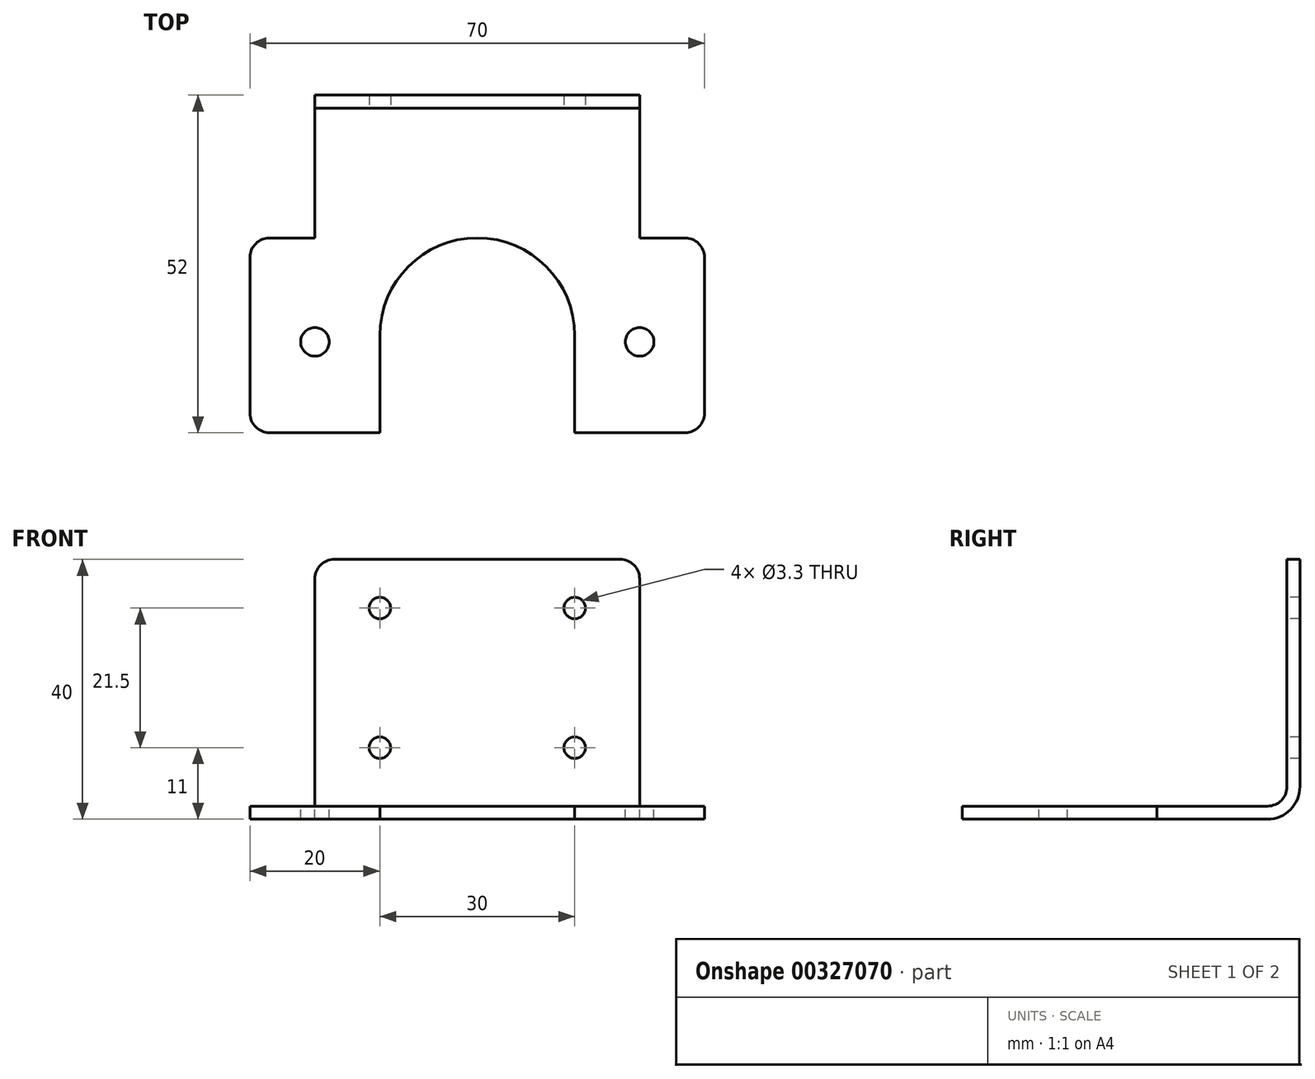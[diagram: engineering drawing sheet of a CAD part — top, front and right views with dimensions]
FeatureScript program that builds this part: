
annotation { "Feature Type Name" : "Feature", "Feature Type Description" : "" }
export const myFeature = defineFeature(function(context is Context, id is Id, definition is map)
    precondition{}
    {
        {
            var Q0;
            Q0=qCreatedBy(makeId("Right.planeOp"),FACE);
            var sketch = newSketch(context, id + "F0", { "sketchPlane" : qUnion([Q0])});
            skLineSegment(sketch, "E0", {"start": v(0, 5) * mm, "end": v(0, 40) * mm});
            skLineSegment(sketch, "E1", {"start": v(-5, 0) * mm, "end": v(-52, 0) * mm});
            skPoint(sketch, "E2.visualSharp", {"position": v(0, 0) * mm});
            skArc(sketch, "E2.filletArc", {"start": v(-5, 0) * mm, "mid": v(-1.46, 1.46) * mm, "end": v(0, 5) * mm});
            skLineSegment(sketch, "E3.0", {"start": v(-2, 5) * mm, "end": v(-2, 40) * mm});
            skArc(sketch, "E3.1", {"start": v(-5, 2) * mm, "mid": v(-2.88, 2.88) * mm, "end": v(-2, 5) * mm});
            skLineSegment(sketch, "E3.2", {"start": v(-5, 2) * mm, "end": v(-52, 2) * mm});
            skLineSegment(sketch, "E4", {"start": v(-52, 2) * mm, "end": v(-52, 0) * mm});
            skLineSegment(sketch, "E5", {"start": v(-2, 40) * mm, "end": v(0, 40) * mm});
            skSolve(sketch);
        }
        {
            var Q0;
            Q0=makeQuery(id+"F0.imprint","IMPRINT",FACE,{"disambiguationData":[TD([[makeQuery(id+"F0.imprint","IMPRINT",EDGE,{"derivedFrom":sQuery(id+"F0.wireOp",EDGE,"E0")}),1.0]])]});
            extrude(context, id + "F1", {"entities" : qUnion([Q0]), "depth" : 50 * mm, "symmetric" : true});
        }
        {
            var Q0;
            Q0=makeQuery(id+"F1.opExtrude","SWEPT_FACE",FACE,{"disambiguationData":[OSD([sQuery(id+"F0.wireOp",EDGE,"E3.0")])]});
            var sketch = newSketch(context, id + "F2", { "sketchPlane" : qUnion([Q0])});
            skLineSegment(sketch, "E6.bottom", {"start": v(15, 32.5) * mm, "end": v(-15, 32.5) * mm});
            skLineSegment(sketch, "E6.top", {"start": v(15, 11) * mm, "end": v(-15, 11) * mm});
            skLineSegment(sketch, "E6.left", {"start": v(15, 32.5) * mm, "end": v(15, 11) * mm});
            skLineSegment(sketch, "E6.right", {"start": v(-15, 32.5) * mm, "end": v(-15, 11) * mm});
            skPoint(sketch, "E6.middle", {"position": v(0, 21.75) * mm});
            skSolve(sketch);
        }
        {
            var Q0;
            Q0=sQuery(id+"F2.wireOp",VERTEX,"E6.right.start");
            var Q1;
            Q1=sQuery(id+"F2.wireOp",VERTEX,"E6.top.end");
            var Q2;
            Q2=sQuery(id+"F2.wireOp",VERTEX,"E6.left.end");
            var Q3;
            Q3=sQuery(id+"F2.wireOp",VERTEX,"E6.left.start");
            var Q4;
            Q4=makeQuery(id+"F1.opExtrude","SWEPT_BODY",BODY,{"disambiguationData":[OSD([sQuery(id+"F0.wireOp",EDGE,"E0"),sQuery(id+"F0.wireOp",EDGE,"E1"),sQuery(id+"F0.wireOp",EDGE,"E2.filletArc"),sQuery(id+"F0.wireOp",EDGE,"E3.0"),sQuery(id+"F0.wireOp",EDGE,"E3.1"),sQuery(id+"F0.wireOp",EDGE,"E3.2"),sQuery(id+"F0.wireOp",EDGE,"E4"),sQuery(id+"F0.wireOp",EDGE,"E5")])]});
            hole(context, id + "F3", {"style" : HoleStyle.SIMPLE, "endStyle" : HoleEndStyle.THROUGH, "standardTappedOrClearance" : lookupTablePath({ "standard" : "ISO", "fit" : "Normal", "size" : "M3", "type" : "Clearance" }), "standardBlindInLast" : lookupTablePath({ "fit" : "Standard", "standard" : "ISO", "size" : "M3", "type" : "Clearance" }), "holeDiameter" : 3.3 * mm, "tappedDepth" : 12 * mm, "tapClearance" : 3, "locations" : qUnion([Q0, Q1, Q2, Q3]), "scope" : qUnion([Q4])});
        }
        {
            var Q0;
            Q0=makeQuery(id+"F1.opExtrude","SWEPT_FACE",FACE,{"disambiguationData":[OSD([sQuery(id+"F0.wireOp",EDGE,"E3.2")])]});
            var sketch = newSketch(context, id + "F4", { "sketchPlane" : qUnion([Q0])});
            skLineSegment(sketch, "E7.bottom", {"start": v(-25, -52) * mm, "end": v(-35, -52) * mm});
            skLineSegment(sketch, "E7.top", {"start": v(-25, -22) * mm, "end": v(-35, -22) * mm});
            skLineSegment(sketch, "E7.left", {"start": v(-25, -52) * mm, "end": v(-25, -22) * mm});
            skLineSegment(sketch, "E7.right", {"start": v(-35, -52) * mm, "end": v(-35, -22) * mm});
            skLineSegment(sketch, "E8", {"start": v(-25, -38) * mm, "end": v(-35, -38) * mm, "construction": true});
            skLineSegment(sketch, "E9.MirrorCS", {"start": v(25, -52) * mm, "end": v(35, -52) * mm});
            skLineSegment(sketch, "E10.MirrorCS", {"start": v(25, -22) * mm, "end": v(35, -22) * mm});
            skLineSegment(sketch, "E11.MirrorCS", {"start": v(25, -52) * mm, "end": v(25, -22) * mm});
            skLineSegment(sketch, "E12.MirrorCS", {"start": v(35, -52) * mm, "end": v(35, -22) * mm});
            skLineSegment(sketch, "E13.MirrorCS", {"start": v(25, -38) * mm, "end": v(35, -38) * mm, "construction": true});
            skCircle(sketch, "E14", {"center": v(0, -37) * mm, "radius": 15 * mm});
            skLineSegment(sketch, "E15", {"start": v(-15, -37) * mm, "end": v(-15, -52) * mm});
            skLineSegment(sketch, "E16", {"start": v(15, -37) * mm, "end": v(15, -52) * mm});
            skSolve(sketch);
        }
        {
            var Q0;
            Q0=makeQuery(id+"F4.imprint","IMPRINT",FACE,{"disambiguationData":[TD([[makeQuery(id+"F4.imprint","IMPRINT",EDGE,{"derivedFrom":sQuery(id+"F4.wireOp",EDGE,"E7.bottom")}),-1.0]])]});
            var Q1;
            Q1=makeQuery(id+"F4.imprint","IMPRINT",FACE,{"disambiguationData":[TD([[makeQuery(id+"F4.imprint","IMPRINT",EDGE,{"derivedFrom":sQuery(id+"F4.wireOp",EDGE,"E9.MirrorCS")}),1.0]])]});
            var Q2;
            Q2=makeQuery(id+"F1.opExtrude","SWEPT_FACE",FACE,{"disambiguationData":[OSD([sQuery(id+"F0.wireOp",EDGE,"E1")])]});
            extrude(context, id + "F5", {"entities" : qUnion([Q0, Q1]), "operationType" : NewBodyOperationType.ADD, "endBound" : BoundingType.UP_TO_SURFACE, "oppositeDirection" : true, "endBoundEntityFace" : qUnion([Q2]), "depth" : 25 * mm});
        }
        {
            var Q0;
            Q0=sQuery(id+"F4.wireOp",VERTEX,"E8.start");
            var Q1;
            Q1=sQuery(id+"F4.wireOp",VERTEX,"E13.MirrorCS.start");
            var Q2;
            Q2=makeQuery(id+"F1.opExtrude","SWEPT_BODY",BODY,{"disambiguationData":[OSD([sQuery(id+"F0.wireOp",EDGE,"E0"),sQuery(id+"F0.wireOp",EDGE,"E1"),sQuery(id+"F0.wireOp",EDGE,"E2.filletArc"),sQuery(id+"F0.wireOp",EDGE,"E3.0"),sQuery(id+"F0.wireOp",EDGE,"E3.1"),sQuery(id+"F0.wireOp",EDGE,"E3.2"),sQuery(id+"F0.wireOp",EDGE,"E4"),sQuery(id+"F0.wireOp",EDGE,"E5")])]});
            hole(context, id + "F6", {"style" : HoleStyle.SIMPLE, "endStyle" : HoleEndStyle.THROUGH, "standardTappedOrClearance" : lookupTablePath({ "standard" : "ISO", "fit" : "Normal", "size" : "M4", "type" : "Clearance" }), "standardBlindInLast" : lookupTablePath({ "fit" : "Standard", "standard" : "ISO", "size" : "M4", "type" : "Clearance" }), "holeDiameter" : 4.4 * mm, "tappedDepth" : 12 * mm, "tapClearance" : 3, "locations" : qUnion([Q0, Q1]), "scope" : qUnion([Q2])});
        }
        {
            var Q0;
            {var subQ0=sQuery(id+"F4.wireOp",EDGE,"E14");var subQ1=makeQuery(id+"F4.imprint","INTERSECT",VERTEX,{"derivedFrom":[subQ0,sQuery(id+"F4.wireOp",EDGE,"E15")]});Q0=makeQuery(id+"F4.imprint","IMPRINT",FACE,{"disambiguationData":[TD([[makeQuery(id+"F4.imprint","IMPRINT",EDGE,{"disambiguationData":[TD([[subQ1,1.0]])],"derivedFrom":subQ0}),1.0]])]});}
            var Q1;
            {var subQ0=sQuery(id+"F4.wireOp",EDGE,"E15");Q1=makeQuery(id+"F4.imprint","IMPRINT",FACE,{"disambiguationData":[TD([[makeQuery(id+"F4.imprint","IMPRINT",EDGE,{"derivedFrom":subQ0}),1.0]])]});}
            var Q2;
            {var subQ0=sQuery(id+"F4.wireOp",EDGE,"E16");Q2=makeQuery(id+"F4.imprint","IMPRINT",FACE,{"disambiguationData":[TD([[makeQuery(id+"F4.imprint","IMPRINT",EDGE,{"derivedFrom":subQ0}),-1.0]])]});}
            extrude(context, id + "F7", {"entities" : qUnion([Q0, Q1, Q2]), "operationType" : NewBodyOperationType.REMOVE, "endBound" : BoundingType.UP_TO_NEXT, "oppositeDirection" : true, "depth" : 25 * mm});
        }
        {
            var Q0;
            Q0=makeQuery(id+"F7.boolean.opBoolean","COPY",EDGE,{"derivedFrom":makeQuery(id+"F7.opExtrude","SWEPT_EDGE",EDGE,{"disambiguationData":[OSD([sQuery(id+"F0.wireOp",EDGE,"E3.2"),sQuery(id+"F0.wireOp",EDGE,"E4"),sQuery(id+"F4.wireOp",EDGE,"E15")])]})});
            var Q1;
            Q1=makeQuery(id+"F5.opExtrude","SWEPT_EDGE",EDGE,{"disambiguationData":[OSD([sQuery(id+"F4.wireOp",EDGE,"E7.bottom"),sQuery(id+"F4.wireOp",EDGE,"E7.right")])]});
            var Q2;
            Q2=makeQuery(id+"F5.opExtrude","SWEPT_EDGE",EDGE,{"disambiguationData":[OSD([sQuery(id+"F4.wireOp",EDGE,"E7.top"),sQuery(id+"F4.wireOp",EDGE,"E7.right")])]});
            var Q3;
            Q3=makeQuery(id+"F5.opExtrude","SWEPT_EDGE",EDGE,{"disambiguationData":[OSD([sQuery(id+"F0.wireOp",EDGE,"E3.2"),sQuery(id+"F4.wireOp",EDGE,"E7.top"),sQuery(id+"F4.wireOp",EDGE,"E7.left")])]});
            var Q4;
            Q4=makeQuery(id+"F1.opExtrude","CAP_EDGE",EDGE,{"disambiguationData":[OSD([sQuery(id+"F0.wireOp",EDGE,"E5")])],"isStart":true});
            var Q5;
            Q5=makeQuery(id+"F7.boolean.opBoolean","COPY",EDGE,{"derivedFrom":makeQuery(id+"F7.opExtrude","SWEPT_EDGE",EDGE,{"disambiguationData":[OSD([sQuery(id+"F0.wireOp",EDGE,"E3.2"),sQuery(id+"F0.wireOp",EDGE,"E4"),sQuery(id+"F4.wireOp",EDGE,"E16")])]})});
            var Q6;
            Q6=makeQuery(id+"F5.opExtrude","SWEPT_EDGE",EDGE,{"disambiguationData":[OSD([sQuery(id+"F4.wireOp",EDGE,"E9.MirrorCS"),sQuery(id+"F4.wireOp",EDGE,"E12.MirrorCS")])]});
            var Q7;
            Q7=makeQuery(id+"F5.opExtrude","SWEPT_EDGE",EDGE,{"disambiguationData":[OSD([sQuery(id+"F4.wireOp",EDGE,"E10.MirrorCS"),sQuery(id+"F4.wireOp",EDGE,"E12.MirrorCS")])]});
            var Q8;
            Q8=makeQuery(id+"F5.opExtrude","SWEPT_EDGE",EDGE,{"disambiguationData":[OSD([sQuery(id+"F0.wireOp",EDGE,"E3.2"),sQuery(id+"F4.wireOp",EDGE,"E10.MirrorCS"),sQuery(id+"F4.wireOp",EDGE,"E11.MirrorCS")])]});
            var Q9;
            Q9=makeQuery(id+"F1.opExtrude","CAP_EDGE",EDGE,{"disambiguationData":[OSD([sQuery(id+"F0.wireOp",EDGE,"E5")])],"isStart":false});
            fillet(context, id + "F8", {"entities" : qUnion([Q0, Q1, Q2, Q3, Q4, Q5, Q6, Q7, Q8, Q9]), "radius" : 3 * mm, "tangentPropagation" : true, "allowEdgeOverflow" : false});
        }
    });
